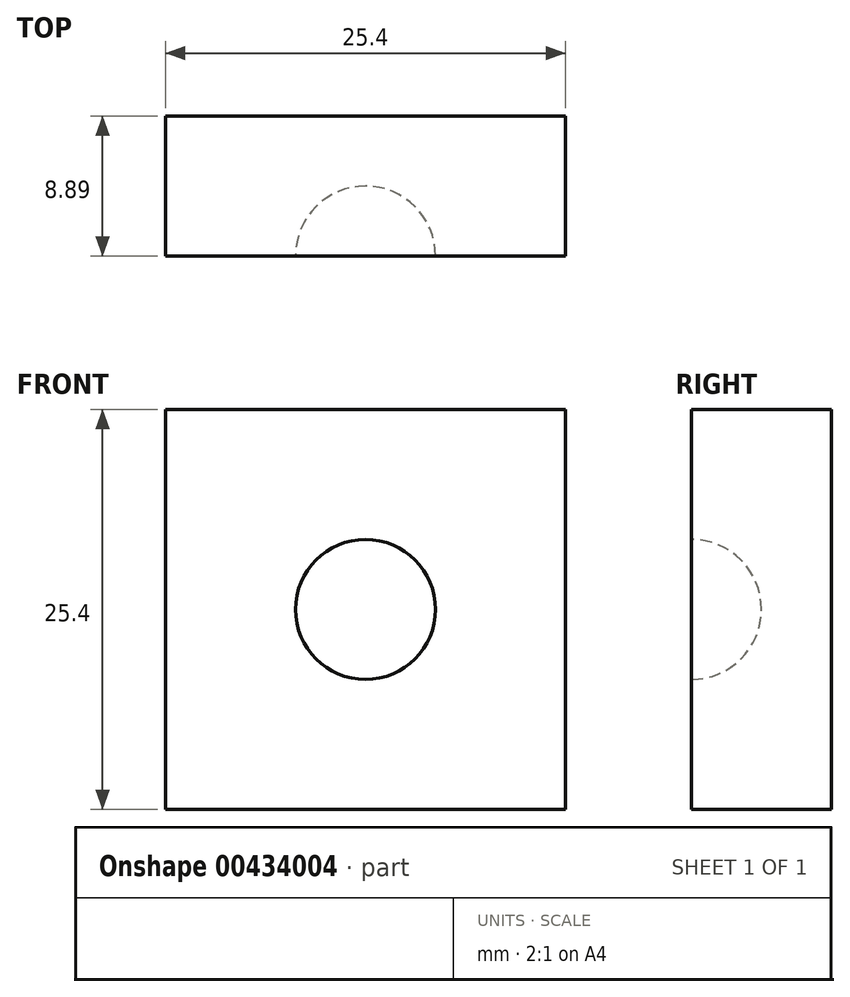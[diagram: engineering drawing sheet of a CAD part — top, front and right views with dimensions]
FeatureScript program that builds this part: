
annotation { "Feature Type Name" : "Feature", "Feature Type Description" : "" }
export const myFeature = defineFeature(function(context is Context, id is Id, definition is map)
    precondition{}
    {
        {
            var Q0;
            Q0=qCreatedBy(makeId("Front.planeOp"),FACE);
            var sketch = newSketch(context, id + "F0", { "sketchPlane" : qUnion([Q0])});
            skLineSegment(sketch, "E0.bottom", {"start": v(-12.7, 12.7) * mm, "end": v(12.7, 12.7) * mm});
            skLineSegment(sketch, "E0.top", {"start": v(-12.7, -12.7) * mm, "end": v(12.7, -12.7) * mm});
            skLineSegment(sketch, "E0.left", {"start": v(-12.7, 12.7) * mm, "end": v(-12.7, -12.7) * mm});
            skLineSegment(sketch, "E0.right", {"start": v(12.7, 12.7) * mm, "end": v(12.7, -12.7) * mm});
            skPoint(sketch, "E0.middle", {"position": v(0, 0) * mm});
            skSolve(sketch);
        }
        {
            var Q0;
            Q0 = qSketchRegion(id + "F0", true);
            extrude(context, id + "F1", {"entities" : qUnion([Q0]), "depth" : 8.9 * mm});
        }
        {
            var Q0;
            Q0=makeQuery(id+"F1.opExtrude","CAP_FACE",FACE,{"disambiguationData":[OSD([sQuery(id+"F0.wireOp",EDGE,"E0.bottom"),sQuery(id+"F0.wireOp",EDGE,"E0.top"),sQuery(id+"F0.wireOp",EDGE,"E0.left"),sQuery(id+"F0.wireOp",EDGE,"E0.right")])],"isStart":false});
            var sketch = newSketch(context, id + "F2", { "sketchPlane" : qUnion([Q0])});
            skArc(sketch, "E1", {"start": v(-4.45, 0) * mm, "mid": v(0, -4.45) * mm, "end": v(4.45, 0) * mm});
            skLineSegment(sketch, "E2", {"start": v(-4.45, 0) * mm, "end": v(4.45, 0) * mm});
            skSolve(sketch);
        }
        {
            var Q0;
            Q0=makeQuery(id+"F2.imprint","IMPRINT",FACE,{"disambiguationData":[TD([[makeQuery(id+"F2.imprint","IMPRINT",EDGE,{"derivedFrom":sQuery(id+"F2.wireOp",EDGE,"E1")}),1.0]])]});
            var Q1;
            Q1=sQuery(id+"F2.wireOp",EDGE,"E2");
            revolve(context, id + "F3", {"operationType" : NewBodyOperationType.REMOVE, "entities" : qUnion([Q0]), "axis" : qUnion([Q1]), "revolveType" : RevolveType.FULL, "oppositeDirection" : true});
        }
    });
